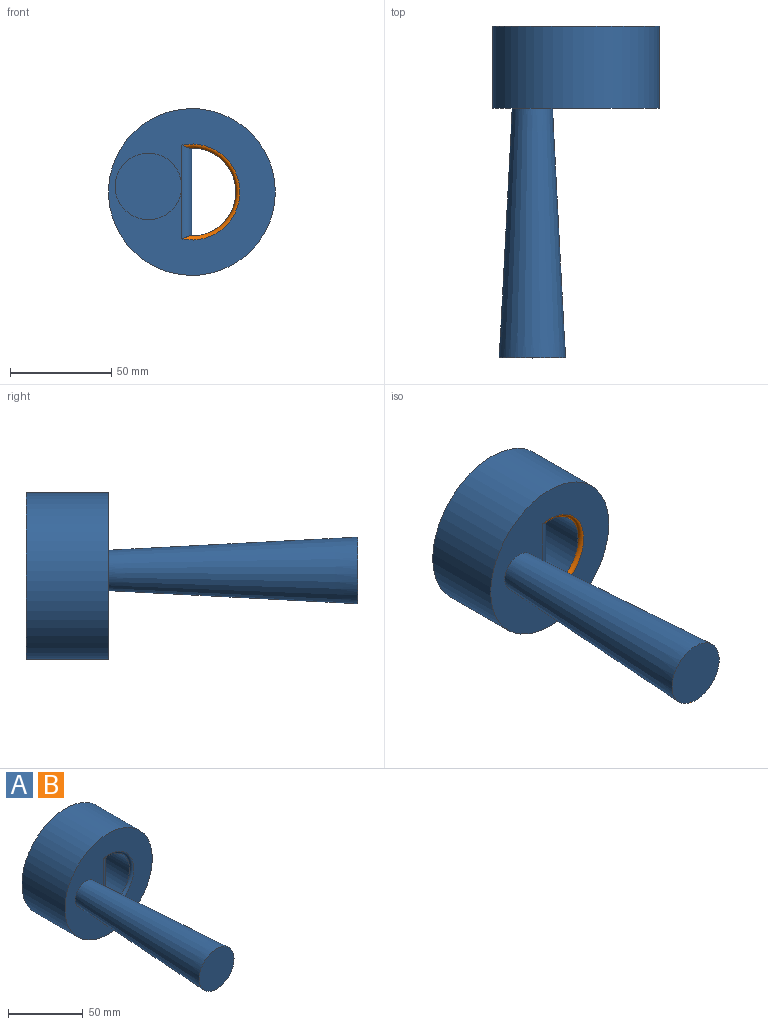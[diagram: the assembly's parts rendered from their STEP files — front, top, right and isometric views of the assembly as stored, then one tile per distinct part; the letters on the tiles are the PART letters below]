
ASSEMBLY  parts=2 mates=1
PART A: 9 faces, bbox 82.5x164.2x82.5 mm
  f0: plane 43.54x35.63mm, normal (1,0,0), area 1551.3mm2, adj f1,f4,f6
  f1: cylinder r=21.77mm len=43.54mm, axis (0,1,0), area 2643.8mm2, adj f0,f4,f5,f6
  f2: cylinder r=41.26mm len=82.52mm, axis (0,1,0), area 10532.3mm2, adj f3,f4
  f3: plane 82.52x82.52mm, normal (0,-1,0), area 3910.1mm2, adj f2,f5,f6,f7
  f4: plane 82.52x82.52mm, normal (0,1,0), area 4603.3mm2, adj f0,f1,f2
  f5: torus R=23.77mm, axis (0,-1,0), area 239.5mm2, adj f1,f3,f6
  f6: cylinder r=5mm len=46.48mm, axis (0,0,-1), area 347mm2, adj f0,f1,f3,f5
  f7: cone r=10mm half-angle=3deg, axis (0,-1,0), area 10293.4mm2, adj f3,f8
  f8: plane 32.96x32.96mm, normal (0,-1,0), area 853mm2, adj f7
PART B: same geometry as A
PLACE A t=(13.33,86.07,-5.6)mm
PLACE B t=(13.33,86.07,-5.6)mm
MATE fastened A.f7 <-> B.f7  axis (0,-1,0) through (-8.22,-78.14,-2.84)mm
